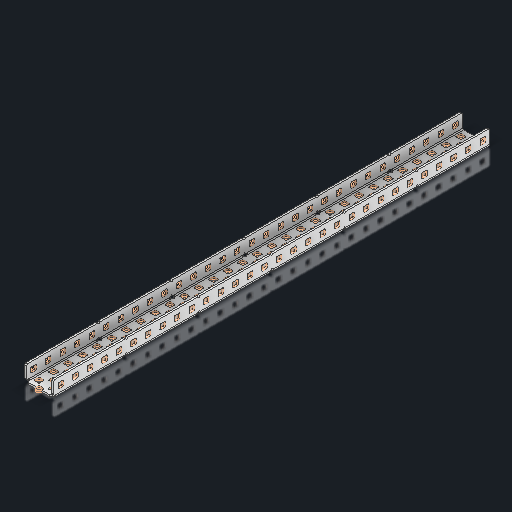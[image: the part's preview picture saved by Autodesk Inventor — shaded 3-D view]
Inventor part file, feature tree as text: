
AUTODESK INVENTOR PART (.ipt)
format: ipt  version: 2023.2 (Build 272271030, 271C)  size: 2,586,112 bytes
history: native  units: in
note: dims shown in document units (in); Inventor stores cm internally (conversion verified against a paired STEP export)
features: other x306, sketch x10, sheet_metal_op x1
ambient origin geometry x8: Origin, YZ Plane, XZ Plane, XY Plane, X Axis, Y Axis, Z Axis, Center Point
bodies: Solid1 (feature_tree)
feature tree (317):
  other  "Alu C 1x2x1x30_MIR_MIR.ipt"
  other  "Solid1::Alu C 1x2x1x30_MIR_MIR.ipt"
  other  "TaggingFeature1"
  sketch  "Sketch1"  dims[d0=0.3937in]
  sketch  "Sketch2"  dims[d1=0.0625in]
  sketch  "Sketch3"
  sketch  "Sketch7"
  other  "Flange Pattern Sketch"
  sketch  "Sketch8"
  sketch  "Sketch9"
  sheet_metal_op  "Body Pattern Sketch"
  sketch  "Sketch15"
  sketch  "Sketch16"
  other  "Arc Length"
  sketch  "Sketch13"
  sketch  "Sketch14"
  other  "Flange Pattern Plane"
  other  "Srf1"
  other  "Srf2"
  other  "Srf3"
  other  "Srf4"
  other  "Srf5"
  other  "Srf6"
  other  "Srf7"
  other  "Srf8"
  other  "Srf9"
  other  "Srf10"
  other  "Srf11"
  other  "Srf12"
  other  "Srf13"
  other  "Srf14"
  other  "Srf15"
  other  "Srf16"
  other  "Srf17"
  other  "Srf18"
  other  "Srf19"
  other  "Srf20"
  other  "Srf21"
  other  "Srf22"
  other  "Srf23"
  other  "Srf24"
  other  "Srf25"
  other  "Srf26"
  other  "Srf27"
  other  "Srf28"
  other  "Srf29"
  other  "Srf30"
  other  "Srf31"
  other  "Srf32"
  other  "Srf33"
  other  "Srf34"
  other  "Srf35"
  other  "Srf36"
  other  "Srf37"
  other  "Srf38"
  other  "Srf39"
  other  "Srf40"
  other  "Srf41"
  other  "Srf42"
  other  "Srf43"
  other  "Srf44"
  other  "Srf45"
  other  "Srf46"
  other  "Srf47"
  other  "Srf48"
  other  "Srf49"
  other  "Srf50"
  other  "Srf51"
  other  "Srf52"
  other  "Srf53"
  other  "Srf54"
  other  "Srf55"
  other  "Srf56"
  other  "Srf57"
  other  "Srf58"
  other  "Srf59"
  other  "Srf60"
  other  "Srf61"
  other  "Srf62"
  other  "Srf63"
  other  "Srf64"
  other  "Srf65"
  other  "Srf66"
  other  "Srf67"
  other  "Srf68"
  other  "Srf69"
  other  "Srf70"
  other  "Srf71"
  other  "Srf72"
  other  "Srf73"
  other  "Srf74"
  other  "Srf75"
  other  "Srf76"
  other  "Srf77"
  other  "Srf78"
  other  "Srf79"
  other  "Srf80"
  other  "Srf81"
  other  "Srf82"
  other  "Srf83"
  other  "Srf84"
  other  "Srf85"
  other  "Srf86"
  other  "Srf87"
  other  "Srf88"
  other  "Srf89"
  other  "Srf90"
  other  "Srf91"
  other  "Srf92"
  other  "Srf93"
  other  "Srf94"
  other  "Srf95"
  other  "Srf96"
  other  "Srf97"
  other  "Srf98"
  other  "Srf99"
  other  "Srf100"
  other  "Srf101"
  other  "Srf102"
  other  "Srf103"
  other  "Srf104"
  other  "Srf105"
  other  "Srf106"
  other  "Srf107"
  other  "Srf108"
  other  "Srf109"
  other  "Srf110"
  other  "Srf111"
  other  "Srf112"
  other  "Srf113"
  other  "Srf114"
  other  "Srf115"
  other  "Srf116"
  other  "Srf117"
  other  "Srf118"
  other  "Srf119"
  other  "Srf120"
  other  "Srf121"
  other  "Srf122"
  other  "Srf123"
  other  "Srf124"
  other  "Srf125"
  other  "Srf126"
  other  "Srf127"
  other  "Srf128"
  other  "Srf129"
  other  "Srf130"
  other  "Srf131"
  other  "Srf132"
  other  "Srf133"
  other  "Srf134"
  other  "Srf135"
  other  "Srf136"
  other  "Srf137"
  other  "Srf138"
  other  "Srf139"
  other  "Srf140"
  other  "Srf141"
  other  "Srf142"
  other  "Srf143"
  other  "Srf144"
  other  "Srf145"
  other  "Srf146"
  other  "Srf147"
  other  "Srf148"
  other  "Srf149"
  other  "Srf150"
  other  "Srf1::Derived"
  other  "Srf2::Derived"
  other  "Srf3::Derived"
  other  "Srf4::Derived"
  other  "Srf5::Derived"
  other  "Srf6::Derived"
  other  "Srf7::Derived"
  other  "Srf8::Derived"
  other  "Srf9::Derived"
  other  "Srf10::Derived"
  other  "Srf11::Derived"
  other  "Srf12::Derived"
  other  "Srf13::Derived"
  other  "Srf14::Derived"
  other  "Srf15::Derived"
  other  "Srf16::Derived"
  other  "Srf17::Derived"
  other  "Srf18::Derived"
  other  "Srf19::Derived"
  other  "Srf20::Derived"
  other  "Srf21::Derived"
  other  "Srf22::Derived"
  other  "Srf23::Derived"
  other  "Srf24::Derived"
  other  "Srf25::Derived"
  other  "Srf26::Derived"
  other  "Srf27::Derived"
  other  "Srf28::Derived"
  other  "Srf29::Derived"
  other  "Srf30::Derived"
  other  "Srf31::Derived"
  other  "Srf32::Derived"
  other  "Srf33::Derived"
  other  "Srf34::Derived"
  other  "Srf35::Derived"
  other  "Srf36::Derived"
  other  "Srf37::Derived"
  other  "Srf38::Derived"
  other  "Srf39::Derived"
  other  "Srf40::Derived"
  other  "Srf41::Derived"
  other  "Srf42::Derived"
  other  "Srf43::Derived"
  other  "Srf44::Derived"
  other  "Srf45::Derived"
  other  "Srf46::Derived"
  other  "Srf47::Derived"
  other  "Srf48::Derived"
  other  "Srf49::Derived"
  other  "Srf50::Derived"
  other  "Srf51::Derived"
  other  "Srf52::Derived"
  other  "Srf53::Derived"
  other  "Srf54::Derived"
  other  "Srf55::Derived"
  other  "Srf56::Derived"
  other  "Srf57::Derived"
  other  "Srf58::Derived"
  other  "Srf59::Derived"
  other  "Srf60::Derived"
  other  "Srf61::Derived"
  other  "Srf62::Derived"
  other  "Srf63::Derived"
  other  "Srf64::Derived"
  other  "Srf65::Derived"
  other  "Srf66::Derived"
  other  "Srf67::Derived"
  other  "Srf68::Derived"
  other  "Srf69::Derived"
  other  "Srf70::Derived"
  other  "Srf71::Derived"
  other  "Srf72::Derived"
  other  "Srf73::Derived"
  other  "Srf74::Derived"
  other  "Srf75::Derived"
  other  "Srf76::Derived"
  other  "Srf77::Derived"
  other  "Srf78::Derived"
  other  "Srf79::Derived"
  other  "Srf80::Derived"
  other  "Srf81::Derived"
  other  "Srf82::Derived"
  other  "Srf83::Derived"
  other  "Srf84::Derived"
  other  "Srf85::Derived"
  other  "Srf86::Derived"
  other  "Srf87::Derived"
  other  "Srf88::Derived"
  other  "Srf89::Derived"
  other  "Srf90::Derived"
  other  "Srf91::Derived"
  other  "Srf92::Derived"
  other  "Srf93::Derived"
  other  "Srf94::Derived"
  other  "Srf95::Derived"
  other  "Srf96::Derived"
  other  "Srf97::Derived"
  other  "Srf98::Derived"
  other  "Srf99::Derived"
  other  "Srf100::Derived"
  other  "Srf101::Derived"
  other  "Srf102::Derived"
  other  "Srf103::Derived"
  other  "Srf104::Derived"
  other  "Srf105::Derived"
  other  "Srf106::Derived"
  other  "Srf107::Derived"
  other  "Srf108::Derived"
  other  "Srf109::Derived"
  other  "Srf110::Derived"
  other  "Srf111::Derived"
  other  "Srf112::Derived"
  other  "Srf113::Derived"
  other  "Srf114::Derived"
  other  "Srf115::Derived"
  other  "Srf116::Derived"
  other  "Srf117::Derived"
  other  "Srf118::Derived"
  other  "Srf119::Derived"
  other  "Srf120::Derived"
  other  "Srf121::Derived"
  other  "Srf122::Derived"
  other  "Srf123::Derived"
  other  "Srf124::Derived"
  other  "Srf125::Derived"
  other  "Srf126::Derived"
  other  "Srf127::Derived"
  other  "Srf128::Derived"
  other  "Srf129::Derived"
  other  "Srf130::Derived"
  other  "Srf131::Derived"
  other  "Srf132::Derived"
  other  "Srf133::Derived"
  other  "Srf134::Derived"
  other  "Srf135::Derived"
  other  "Srf136::Derived"
  other  "Srf137::Derived"
  other  "Srf138::Derived"
  other  "Srf139::Derived"
  other  "Srf140::Derived"
  other  "Srf141::Derived"
  other  "Srf142::Derived"
  other  "Srf143::Derived"
  other  "Srf144::Derived"
  other  "Srf145::Derived"
  other  "Srf146::Derived"
  other  "Srf147::Derived"
  other  "Srf148::Derived"
  other  "Srf149::Derived"
  other  "Srf150::Derived"
